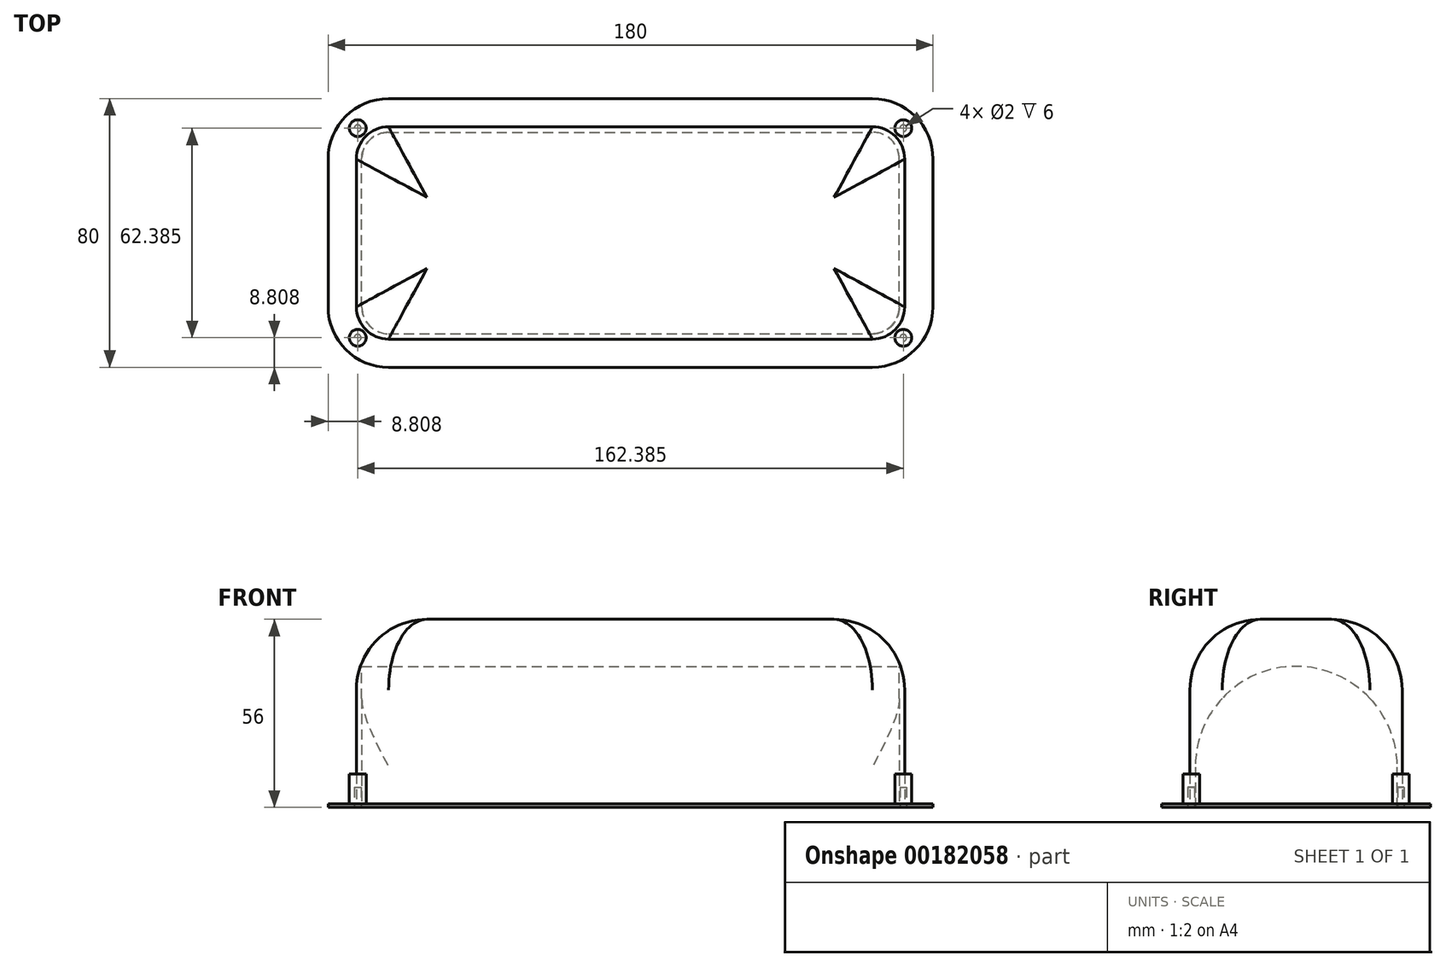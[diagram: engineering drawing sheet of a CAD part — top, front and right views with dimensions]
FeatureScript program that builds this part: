
annotation { "Feature Type Name" : "Feature", "Feature Type Description" : "" }
export const myFeature = defineFeature(function(context is Context, id is Id, definition is map)
    precondition{}
    {
        {
            var Q0;
            Q0=qCreatedBy(makeId("Top.planeOp"),FACE);
            var sketch = newSketch(context, id + "F0", { "sketchPlane" : qUnion([Q0])});
            skLineSegment(sketch, "E0.bottom", {"start": v(72, -40) * mm, "end": v(-72, -40) * mm});
            skLineSegment(sketch, "E0.top", {"start": v(72, 40) * mm, "end": v(-72, 40) * mm});
            skLineSegment(sketch, "E0.left", {"start": v(90, -22) * mm, "end": v(90, 22) * mm});
            skLineSegment(sketch, "E0.right", {"start": v(-90, -22) * mm, "end": v(-90, 22) * mm});
            skPoint(sketch, "E0.middle", {"position": v(0, 0) * mm});
            skPoint(sketch, "E1.visualSharp", {"position": v(-90, 40) * mm});
            skArc(sketch, "E1.filletArc", {"start": v(-72, 40) * mm, "mid": v(-84.73, 34.73) * mm, "end": v(-90, 22) * mm});
            skPoint(sketch, "E2.visualSharp", {"position": v(-90, -40) * mm});
            skArc(sketch, "E2.filletArc", {"start": v(-90, -22) * mm, "mid": v(-84.73, -34.73) * mm, "end": v(-72, -40) * mm});
            skPoint(sketch, "E3.visualSharp", {"position": v(90, -40) * mm});
            skArc(sketch, "E3.filletArc", {"start": v(72, -40) * mm, "mid": v(84.73, -34.73) * mm, "end": v(90, -22) * mm});
            skPoint(sketch, "E4.visualSharp", {"position": v(90, 40) * mm});
            skArc(sketch, "E4.filletArc", {"start": v(90, 22) * mm, "mid": v(84.73, 34.73) * mm, "end": v(72, 40) * mm});
            skLineSegment(sketch, "E5.0", {"start": v(72, 30) * mm, "end": v(-72, 30) * mm});
            skArc(sketch, "E5.1", {"start": v(80, 22) * mm, "mid": v(77.66, 27.66) * mm, "end": v(72, 30) * mm});
            skArc(sketch, "E5.2", {"start": v(-72, 30) * mm, "mid": v(-77.66, 27.66) * mm, "end": v(-80, 22) * mm});
            skLineSegment(sketch, "E5.3", {"start": v(80, -22) * mm, "end": v(80, 22) * mm});
            skLineSegment(sketch, "E5.4", {"start": v(-80, -22) * mm, "end": v(-80, 22) * mm});
            skArc(sketch, "E5.5", {"start": v(-80, -22) * mm, "mid": v(-77.66, -27.66) * mm, "end": v(-72, -30) * mm});
            skLineSegment(sketch, "E5.6", {"start": v(72, -30) * mm, "end": v(-72, -30) * mm});
            skArc(sketch, "E5.7", {"start": v(72, -30) * mm, "mid": v(77.66, -27.66) * mm, "end": v(80, -22) * mm});
            skSolve(sketch);
        }
        {
            var Q0;
            Q0 = qSketchRegion(id + "F0", true);
            extrude(context, id + "F1", {"entities" : qUnion([Q0]), "depth" : 1 * mm});
        }
        {
            var Q0;
            Q0=makeQuery(id+"F1.opExtrude","CAP_FACE",FACE,{"disambiguationData":[OSD([sQuery(id+"F0.wireOp",EDGE,"E0.bottom"),sQuery(id+"F0.wireOp",EDGE,"E0.top"),sQuery(id+"F0.wireOp",EDGE,"E0.left"),sQuery(id+"F0.wireOp",EDGE,"E0.right"),sQuery(id+"F0.wireOp",EDGE,"E1.filletArc"),sQuery(id+"F0.wireOp",EDGE,"E2.filletArc"),sQuery(id+"F0.wireOp",EDGE,"E3.filletArc"),sQuery(id+"F0.wireOp",EDGE,"E4.filletArc"),sQuery(id+"F0.wireOp",EDGE,"E5.0"),sQuery(id+"F0.wireOp",EDGE,"E5.1"),sQuery(id+"F0.wireOp",EDGE,"E5.2"),sQuery(id+"F0.wireOp",EDGE,"E5.3"),sQuery(id+"F0.wireOp",EDGE,"E5.4"),sQuery(id+"F0.wireOp",EDGE,"E5.5"),sQuery(id+"F0.wireOp",EDGE,"E5.6"),sQuery(id+"F0.wireOp",EDGE,"E5.7")])],"isStart":false});
            var sketch = newSketch(context, id + "F2", { "sketchPlane" : qUnion([Q0])});
            skLineSegment(sketch, "E6.0", {"start": v(72, 30) * mm, "end": v(-72, 30) * mm});
            skArc(sketch, "E7.0", {"start": v(-72, 30) * mm, "mid": v(-77.66, 27.66) * mm, "end": v(-80, 22) * mm});
            skLineSegment(sketch, "E8.0", {"start": v(-80, -22) * mm, "end": v(-80, 22) * mm});
            skArc(sketch, "E9.0", {"start": v(-80, -22) * mm, "mid": v(-77.66, -27.66) * mm, "end": v(-72, -30) * mm});
            skLineSegment(sketch, "E10.0", {"start": v(72, -30) * mm, "end": v(-72, -30) * mm});
            skArc(sketch, "E11.0", {"start": v(72, -30) * mm, "mid": v(77.66, -27.66) * mm, "end": v(80, -22) * mm});
            skLineSegment(sketch, "E12.0", {"start": v(80, -22) * mm, "end": v(80, 22) * mm});
            skArc(sketch, "E13.0", {"start": v(80, 22) * mm, "mid": v(77.66, 27.66) * mm, "end": v(72, 30) * mm});
            skArc(sketch, "E14.0", {"start": v(81.6, 22) * mm, "mid": v(78.79, 28.79) * mm, "end": v(72, 31.6) * mm});
            skLineSegment(sketch, "E14.1", {"start": v(81.6, -22) * mm, "end": v(81.6, 22) * mm});
            skLineSegment(sketch, "E14.2", {"start": v(72, 31.6) * mm, "end": v(-72, 31.6) * mm});
            skArc(sketch, "E14.3", {"start": v(72, -31.6) * mm, "mid": v(78.79, -28.79) * mm, "end": v(81.6, -22) * mm});
            skArc(sketch, "E14.4", {"start": v(-72, 31.6) * mm, "mid": v(-78.79, 28.79) * mm, "end": v(-81.6, 22) * mm});
            skLineSegment(sketch, "E14.5", {"start": v(-81.6, -22) * mm, "end": v(-81.6, 22) * mm});
            skArc(sketch, "E14.6", {"start": v(-81.6, -22) * mm, "mid": v(-78.79, -28.79) * mm, "end": v(-72, -31.6) * mm});
            skLineSegment(sketch, "E14.7", {"start": v(72, -31.6) * mm, "end": v(-72, -31.6) * mm});
            skArc(sketch, "E15.0", {"start": v(-85, -22) * mm, "mid": v(-81.2, -31.2) * mm, "end": v(-72, -35) * mm});
            skLineSegment(sketch, "E15.1", {"start": v(-85, 22) * mm, "end": v(-85, -22) * mm});
            skLineSegment(sketch, "E15.2", {"start": v(-72, -35) * mm, "end": v(72, -35) * mm});
            skArc(sketch, "E15.3", {"start": v(-72, 35) * mm, "mid": v(-81.2, 31.2) * mm, "end": v(-85, 22) * mm});
            skArc(sketch, "E15.4", {"start": v(72, -35) * mm, "mid": v(81.2, -31.2) * mm, "end": v(85, -22) * mm});
            skLineSegment(sketch, "E15.5", {"start": v(85, -22) * mm, "end": v(85, 22) * mm});
            skArc(sketch, "E15.6", {"start": v(85, 22) * mm, "mid": v(81.2, 31.2) * mm, "end": v(72, 35) * mm});
            skLineSegment(sketch, "E15.7", {"start": v(72, 35) * mm, "end": v(-72, 35) * mm});
            skSolve(sketch);
        }
        {
            var Q0;
            Q0=makeQuery(id+"F2.imprint","IMPRINT",FACE,{"disambiguationData":[TD([[makeQuery(id+"F2.imprint","IMPRINT",EDGE,{"derivedFrom":sQuery(id+"F2.wireOp",EDGE,"E6.0")}),-1.0]])]});
            extrude(context, id + "F3", {"entities" : qUnion([Q0]), "operationType" : NewBodyOperationType.ADD, "depth" : 55 * mm});
        }
        {
            var Q0;
            Q0=makeQuery(id+"F1.opExtrude","CAP_FACE",FACE,{"disambiguationData":[OSD([sQuery(id+"F0.wireOp",EDGE,"E0.bottom"),sQuery(id+"F0.wireOp",EDGE,"E0.top"),sQuery(id+"F0.wireOp",EDGE,"E0.left"),sQuery(id+"F0.wireOp",EDGE,"E0.right"),sQuery(id+"F0.wireOp",EDGE,"E1.filletArc"),sQuery(id+"F0.wireOp",EDGE,"E2.filletArc"),sQuery(id+"F0.wireOp",EDGE,"E3.filletArc"),sQuery(id+"F0.wireOp",EDGE,"E4.filletArc"),sQuery(id+"F0.wireOp",EDGE,"E5.0"),sQuery(id+"F0.wireOp",EDGE,"E5.1"),sQuery(id+"F0.wireOp",EDGE,"E5.2"),sQuery(id+"F0.wireOp",EDGE,"E5.3"),sQuery(id+"F0.wireOp",EDGE,"E5.4"),sQuery(id+"F0.wireOp",EDGE,"E5.5"),sQuery(id+"F0.wireOp",EDGE,"E5.6"),sQuery(id+"F0.wireOp",EDGE,"E5.7")])],"isStart":true});
            var sketch = newSketch(context, id + "F4", { "sketchPlane" : qUnion([Q0])});
            skLineSegment(sketch, "E16", {"start": v(-77.66, -27.66) * mm, "end": v(-84.73, -34.73) * mm});
            skLineSegment(sketch, "E17", {"start": v(77.66, -27.66) * mm, "end": v(84.73, -34.73) * mm});
            skLineSegment(sketch, "E18", {"start": v(77.66, 27.66) * mm, "end": v(84.73, 34.73) * mm});
            skLineSegment(sketch, "E19", {"start": v(-77.66, 27.66) * mm, "end": v(-84.73, 34.73) * mm});
            skCircle(sketch, "E20", {"center": v(81.2, -31.2) * mm, "radius": 2.5 * mm});
            skCircle(sketch, "E21", {"center": v(-81.2, -31.2) * mm, "radius": 2.5 * mm});
            skCircle(sketch, "E22", {"center": v(81.2, 31.2) * mm, "radius": 2.5 * mm});
            skCircle(sketch, "E23", {"center": v(-81.2, 31.2) * mm, "radius": 2.5 * mm});
            skSolve(sketch);
        }
        {
            var Q0;
            Q0 = qSketchRegion(id + "F4", true);
            extrude(context, id + "F5", {"entities" : qUnion([Q0]), "operationType" : NewBodyOperationType.ADD, "oppositeDirection" : true, "depth" : 10 * mm});
        }
        {
            var Q0;
            Q0=qCreatedBy(makeId("Right.planeOp"),FACE);
            var sketch = newSketch(context, id + "F6", { "sketchPlane" : qUnion([Q0])});
            skLineSegment(sketch, "E24.0", {"start": v(-22, 0) * mm, "end": v(22, 0) * mm});
            skLineSegment(sketch, "E25.0", {"start": v(-30, 0) * mm, "end": v(-22, 0) * mm});
            skLineSegment(sketch, "E26.0", {"start": v(22, 0) * mm, "end": v(30, 0) * mm});
            skLineSegment(sketch, "E27", {"start": v(0, 0) * mm, "end": v(0, 42) * mm});
            skLineSegment(sketch, "E28", {"start": v(-30, 0) * mm, "end": v(-30, 2) * mm});
            skLineSegment(sketch, "E29", {"start": v(-30, 2) * mm, "end": v(-30, 12) * mm});
            skLineSegment(sketch, "E30", {"start": v(0, 42) * mm, "end": v(0, 42) * mm});
            skLineSegment(sketch, "E31", {"start": v(30, 12) * mm, "end": v(30, 2) * mm});
            skLineSegment(sketch, "E32", {"start": v(30, 2) * mm, "end": v(30, 0) * mm});
            skPoint(sketch, "E33.visualSharp", {"position": v(-30, 42) * mm});
            skArc(sketch, "E33.filletArc", {"start": v(0, 42) * mm, "mid": v(-21.21, 33.21) * mm, "end": v(-30, 12) * mm});
            skPoint(sketch, "E34.visualSharp", {"position": v(30, 42) * mm});
            skArc(sketch, "E34.filletArc", {"start": v(30, 12) * mm, "mid": v(21.21, 33.21) * mm, "end": v(0, 42) * mm});
            skLineSegment(sketch, "E35", {"start": v(-30, 12) * mm, "end": v(-30, 56) * mm});
            skLineSegment(sketch, "E36", {"start": v(-30, 56) * mm, "end": v(30, 56) * mm});
            skLineSegment(sketch, "E37", {"start": v(30, 56) * mm, "end": v(30, 12) * mm});
            skSolve(sketch);
        }
        {
            var Q0;
            Q0=makeQuery(id+"F6.imprint","IMPRINT",FACE,{"disambiguationData":[TD([[makeQuery(id+"F6.imprint","IMPRINT",EDGE,{"derivedFrom":sQuery(id+"F6.wireOp",EDGE,"E33.filletArc")}),-1.0]])]});
            extrude(context, id + "F7", {"entities" : qUnion([Q0]), "operationType" : NewBodyOperationType.ADD, "oppositeDirection" : true, "depth" : 3.2 * mm, "hasSecondDirection" : true, "secondDirectionOppositeDirection" : false, "secondDirectionDepth" : 3.2 * mm});
        }
        {
            var Q0;
            Q0=makeQuery(id+"F7.boolean.opBoolean","MERGE",FACE,{"derivedFrom":[makeQuery(id+"F3.opExtrude","CAP_FACE",FACE,{"disambiguationData":[OSD([sQuery(id+"F2.wireOp",EDGE,"E6.0"),sQuery(id+"F2.wireOp",EDGE,"E7.0"),sQuery(id+"F2.wireOp",EDGE,"E8.0"),sQuery(id+"F2.wireOp",EDGE,"E9.0"),sQuery(id+"F2.wireOp",EDGE,"E10.0"),sQuery(id+"F2.wireOp",EDGE,"E11.0"),sQuery(id+"F2.wireOp",EDGE,"E12.0"),sQuery(id+"F2.wireOp",EDGE,"E13.0"),sQuery(id+"F2.wireOp",EDGE,"E14.0"),sQuery(id+"F2.wireOp",EDGE,"E14.1"),sQuery(id+"F2.wireOp",EDGE,"E14.2"),sQuery(id+"F2.wireOp",EDGE,"E14.3"),sQuery(id+"F2.wireOp",EDGE,"E14.4"),sQuery(id+"F2.wireOp",EDGE,"E14.5"),sQuery(id+"F2.wireOp",EDGE,"E14.6"),sQuery(id+"F2.wireOp",EDGE,"E14.7")])],"isStart":false}),makeQuery(id+"F7.opExtrude","SWEPT_FACE",FACE,{"disambiguationData":[OSD([sQuery(id+"F6.wireOp",EDGE,"E36")])]})]});
            var sketch = newSketch(context, id + "F8", { "sketchPlane" : qUnion([Q0])});
            skArc(sketch, "E38.0", {"start": v(72, -31.6) * mm, "mid": v(78.79, -28.79) * mm, "end": v(81.6, -22) * mm});
            skLineSegment(sketch, "E39.0", {"start": v(72, -31.6) * mm, "end": v(-72, -31.6) * mm});
            skLineSegment(sketch, "E40.0", {"start": v(81.6, -22) * mm, "end": v(81.6, 22) * mm});
            skArc(sketch, "E41.0", {"start": v(81.6, 22) * mm, "mid": v(78.79, 28.79) * mm, "end": v(72, 31.6) * mm});
            skLineSegment(sketch, "E42.0", {"start": v(72, 31.6) * mm, "end": v(-72, 31.6) * mm});
            skArc(sketch, "E43.0", {"start": v(-72, 31.6) * mm, "mid": v(-78.79, 28.79) * mm, "end": v(-81.6, 22) * mm});
            skLineSegment(sketch, "E44.0", {"start": v(-81.6, -22) * mm, "end": v(-81.6, 22) * mm});
            skArc(sketch, "E45.0", {"start": v(-81.6, -22) * mm, "mid": v(-78.79, -28.79) * mm, "end": v(-72, -31.6) * mm});
            skSolve(sketch);
        }
        {
            var Q0;
            Q0=makeQuery(id+"F1.opExtrude","CAP_FACE",FACE,{"disambiguationData":[OSD([sQuery(id+"F0.wireOp",EDGE,"E0.bottom"),sQuery(id+"F0.wireOp",EDGE,"E0.top"),sQuery(id+"F0.wireOp",EDGE,"E0.left"),sQuery(id+"F0.wireOp",EDGE,"E0.right"),sQuery(id+"F0.wireOp",EDGE,"E1.filletArc"),sQuery(id+"F0.wireOp",EDGE,"E2.filletArc"),sQuery(id+"F0.wireOp",EDGE,"E3.filletArc"),sQuery(id+"F0.wireOp",EDGE,"E4.filletArc"),sQuery(id+"F0.wireOp",EDGE,"E5.0"),sQuery(id+"F0.wireOp",EDGE,"E5.1"),sQuery(id+"F0.wireOp",EDGE,"E5.2"),sQuery(id+"F0.wireOp",EDGE,"E5.3"),sQuery(id+"F0.wireOp",EDGE,"E5.4"),sQuery(id+"F0.wireOp",EDGE,"E5.5"),sQuery(id+"F0.wireOp",EDGE,"E5.6"),sQuery(id+"F0.wireOp",EDGE,"E5.7")])],"isStart":true});
            var sketch = newSketch(context, id + "F9", { "sketchPlane" : qUnion([Q0])});
            skLineSegment(sketch, "E46.0", {"start": v(72, 40) * mm, "end": v(-72, 40) * mm});
            skArc(sketch, "E47.0", {"start": v(-90, 22) * mm, "mid": v(-84.73, 34.73) * mm, "end": v(-72, 40) * mm});
            skLineSegment(sketch, "E48.0", {"start": v(-90, 22) * mm, "end": v(-90, -22) * mm});
            skArc(sketch, "E49.0", {"start": v(-72, -40) * mm, "mid": v(-84.73, -34.73) * mm, "end": v(-90, -22) * mm});
            skLineSegment(sketch, "E50.0", {"start": v(72, -40) * mm, "end": v(-72, -40) * mm});
            skArc(sketch, "E51.0", {"start": v(90, -22) * mm, "mid": v(84.73, -34.73) * mm, "end": v(72, -40) * mm});
            skLineSegment(sketch, "E52.0", {"start": v(90, 22) * mm, "end": v(90, -22) * mm});
            skArc(sketch, "E53.0", {"start": v(72, 40) * mm, "mid": v(84.73, 34.73) * mm, "end": v(90, 22) * mm});
            skArc(sketch, "E54.0", {"start": v(72, 40.8) * mm, "mid": v(85.3, 35.3) * mm, "end": v(90.8, 22) * mm});
            skLineSegment(sketch, "E54.1", {"start": v(90.8, 22) * mm, "end": v(90.8, -22) * mm});
            skLineSegment(sketch, "E54.2", {"start": v(72, 40.8) * mm, "end": v(-72, 40.8) * mm});
            skArc(sketch, "E54.3", {"start": v(90.8, -22) * mm, "mid": v(85.3, -35.3) * mm, "end": v(72, -40.8) * mm});
            skArc(sketch, "E54.4", {"start": v(-90.8, 22) * mm, "mid": v(-85.3, 35.3) * mm, "end": v(-72, 40.8) * mm});
            skLineSegment(sketch, "E54.5", {"start": v(-90.8, 22) * mm, "end": v(-90.8, -22) * mm});
            skArc(sketch, "E54.6", {"start": v(-72, -40.8) * mm, "mid": v(-85.3, -35.3) * mm, "end": v(-90.8, -22) * mm});
            skLineSegment(sketch, "E54.7", {"start": v(72, -40.8) * mm, "end": v(-72, -40.8) * mm});
            skSolve(sketch);
        }
        {
            var Q0;
            Q0=makeQuery(id+"FBeGWCSvGBcqAvT_1.boolean.opBoolean","MERGE",FACE,{"derivedFrom":[makeQuery(id+"F1.opExtrude","CAP_FACE",FACE,{"disambiguationData":[OSD([sQuery(id+"F0.wireOp",EDGE,"E0.bottom"),sQuery(id+"F0.wireOp",EDGE,"E0.top"),sQuery(id+"F0.wireOp",EDGE,"E0.left"),sQuery(id+"F0.wireOp",EDGE,"E0.right"),sQuery(id+"F0.wireOp",EDGE,"E1.filletArc"),sQuery(id+"F0.wireOp",EDGE,"E2.filletArc"),sQuery(id+"F0.wireOp",EDGE,"E3.filletArc"),sQuery(id+"F0.wireOp",EDGE,"E4.filletArc"),sQuery(id+"F0.wireOp",EDGE,"E5.0"),sQuery(id+"F0.wireOp",EDGE,"E5.1"),sQuery(id+"F0.wireOp",EDGE,"E5.2"),sQuery(id+"F0.wireOp",EDGE,"E5.3"),sQuery(id+"F0.wireOp",EDGE,"E5.4"),sQuery(id+"F0.wireOp",EDGE,"E5.5"),sQuery(id+"F0.wireOp",EDGE,"E5.6"),sQuery(id+"F0.wireOp",EDGE,"E5.7")])],"isStart":true}),makeQuery(id+"FBeGWCSvGBcqAvT_1.opExtrude","CAP_FACE",FACE,{"disambiguationData":[OSD([sQuery(id+"F9.wireOp",EDGE,"E46.0"),sQuery(id+"F9.wireOp",EDGE,"E47.0"),sQuery(id+"F9.wireOp",EDGE,"E48.0"),sQuery(id+"F9.wireOp",EDGE,"E49.0"),sQuery(id+"F9.wireOp",EDGE,"E50.0"),sQuery(id+"F9.wireOp",EDGE,"E51.0"),sQuery(id+"F9.wireOp",EDGE,"E52.0"),sQuery(id+"F9.wireOp",EDGE,"E53.0"),sQuery(id+"F9.wireOp",EDGE,"E54.0"),sQuery(id+"F9.wireOp",EDGE,"E54.1"),sQuery(id+"F9.wireOp",EDGE,"E54.2"),sQuery(id+"F9.wireOp",EDGE,"E54.3"),sQuery(id+"F9.wireOp",EDGE,"E54.4"),sQuery(id+"F9.wireOp",EDGE,"E54.5"),sQuery(id+"F9.wireOp",EDGE,"E54.6"),sQuery(id+"F9.wireOp",EDGE,"E54.7")])],"isStart":true})]});
            var sketch = newSketch(context, id + "F10", { "sketchPlane" : qUnion([Q0])});
            skCircle(sketch, "E55.0", {"center": v(-81.2, 31.2) * mm, "radius": 2.5 * mm});
            skCircle(sketch, "E56.0", {"center": v(-81.2, -31.2) * mm, "radius": 2.5 * mm});
            skCircle(sketch, "E57.0", {"center": v(81.2, 31.2) * mm, "radius": 2.5 * mm});
            skCircle(sketch, "E58.0", {"center": v(81.2, -31.2) * mm, "radius": 2.5 * mm});
            skCircle(sketch, "E59", {"center": v(81.2, 31.2) * mm, "radius": 1 * mm});
            skCircle(sketch, "E60", {"center": v(81.2, -31.2) * mm, "radius": 1 * mm});
            skCircle(sketch, "E61", {"center": v(-81.2, 31.2) * mm, "radius": 1 * mm});
            skCircle(sketch, "E62", {"center": v(-81.2, -31.2) * mm, "radius": 1 * mm});
            skSolve(sketch);
        }
        {
            var Q0;
            Q0=makeQuery(id+"F10.imprint","IMPRINT",FACE,{"disambiguationData":[TD([[makeQuery(id+"F10.imprint","IMPRINT",EDGE,{"derivedFrom":sQuery(id+"F10.wireOp",EDGE,"E61")}),1.0]])]});
            var Q1;
            Q1=makeQuery(id+"F10.imprint","IMPRINT",FACE,{"disambiguationData":[TD([[makeQuery(id+"F10.imprint","IMPRINT",EDGE,{"derivedFrom":sQuery(id+"F10.wireOp",EDGE,"E62")}),1.0]])]});
            var Q2;
            Q2=makeQuery(id+"F10.imprint","IMPRINT",FACE,{"disambiguationData":[TD([[makeQuery(id+"F10.imprint","IMPRINT",EDGE,{"derivedFrom":sQuery(id+"F10.wireOp",EDGE,"E60")}),1.0]])]});
            var Q3;
            Q3=makeQuery(id+"F10.imprint","IMPRINT",FACE,{"disambiguationData":[TD([[makeQuery(id+"F10.imprint","IMPRINT",EDGE,{"derivedFrom":sQuery(id+"F10.wireOp",EDGE,"E59")}),1.0]])]});
            extrude(context, id + "F11", {"entities" : qUnion([Q0, Q1, Q2, Q3]), "operationType" : NewBodyOperationType.REMOVE, "oppositeDirection" : true, "depth" : 6 * mm});
        }
        {
            var Q0;
            Q0=makeQuery(id+"F7.opExtrude","CAP_FACE",FACE,{"disambiguationData":[OSD([sQuery(id+"F6.wireOp",EDGE,"E33.filletArc"),sQuery(id+"F6.wireOp",EDGE,"E34.filletArc"),sQuery(id+"F6.wireOp",EDGE,"E35"),sQuery(id+"F6.wireOp",EDGE,"E36"),sQuery(id+"F6.wireOp",EDGE,"E37")])],"isStart":false});
            var sketch = newSketch(context, id + "F12", { "sketchPlane" : qUnion([Q0])});
            skArc(sketch, "E63.0.0", {"start": v(-30, 12) * mm, "mid": v(0, 42) * mm, "end": v(30, 12) * mm});
            skLineSegment(sketch, "E63.0.1", {"start": v(30, 12) * mm, "end": v(30, 56) * mm});
            skLineSegment(sketch, "E63.0.2", {"start": v(30, 56) * mm, "end": v(-30, 56) * mm});
            skLineSegment(sketch, "E63.0.3", {"start": v(-30, 56) * mm, "end": v(-30, 12) * mm});
            skSolve(sketch);
        }
        {
            var Q0;
            Q0 = qSketchRegion(id + "F12", true);
            var Q1;
            Q1=makeQuery(id+"F1.opExtrude","SWEPT_BODY",BODY,{"disambiguationData":[OSD([sQuery(id+"F0.wireOp",EDGE,"E0.bottom"),sQuery(id+"F0.wireOp",EDGE,"E0.top"),sQuery(id+"F0.wireOp",EDGE,"E0.left"),sQuery(id+"F0.wireOp",EDGE,"E0.right"),sQuery(id+"F0.wireOp",EDGE,"E1.filletArc"),sQuery(id+"F0.wireOp",EDGE,"E2.filletArc"),sQuery(id+"F0.wireOp",EDGE,"E3.filletArc"),sQuery(id+"F0.wireOp",EDGE,"E4.filletArc"),sQuery(id+"F0.wireOp",EDGE,"E5.0"),sQuery(id+"F0.wireOp",EDGE,"E5.1"),sQuery(id+"F0.wireOp",EDGE,"E5.2"),sQuery(id+"F0.wireOp",EDGE,"E5.3"),sQuery(id+"F0.wireOp",EDGE,"E5.4"),sQuery(id+"F0.wireOp",EDGE,"E5.5"),sQuery(id+"F0.wireOp",EDGE,"E5.6"),sQuery(id+"F0.wireOp",EDGE,"E5.7")])]});
            extrude(context, id + "F13", {"entities" : qUnion([Q0]), "operationType" : NewBodyOperationType.ADD, "endBound" : BoundingType.UP_TO_BODY, "endBoundEntityBody" : qUnion([Q1]), "depth" : 25 * mm});
        }
        {
            var Q0;
            Q0=makeQuery(id+"F7.opExtrude","CAP_FACE",FACE,{"disambiguationData":[OSD([sQuery(id+"F6.wireOp",EDGE,"E33.filletArc"),sQuery(id+"F6.wireOp",EDGE,"E34.filletArc"),sQuery(id+"F6.wireOp",EDGE,"E35"),sQuery(id+"F6.wireOp",EDGE,"E36"),sQuery(id+"F6.wireOp",EDGE,"E37")])],"isStart":true});
            var sketch = newSketch(context, id + "F14", { "sketchPlane" : qUnion([Q0])});
            skArc(sketch, "E64.0.0", {"start": v(-30, 12) * mm, "mid": v(0, 42) * mm, "end": v(30, 12) * mm});
            skLineSegment(sketch, "E64.0.1", {"start": v(30, 12) * mm, "end": v(30, 56) * mm});
            skLineSegment(sketch, "E64.0.2", {"start": v(30, 56) * mm, "end": v(-30, 56) * mm});
            skLineSegment(sketch, "E64.0.3", {"start": v(-30, 56) * mm, "end": v(-30, 12) * mm});
            skSolve(sketch);
        }
        {
            var Q0;
            Q0 = qSketchRegion(id + "F14", true);
            var Q1;
            Q1=makeQuery(id+"F1.opExtrude","SWEPT_BODY",BODY,{"disambiguationData":[OSD([sQuery(id+"F0.wireOp",EDGE,"E0.bottom"),sQuery(id+"F0.wireOp",EDGE,"E0.top"),sQuery(id+"F0.wireOp",EDGE,"E0.left"),sQuery(id+"F0.wireOp",EDGE,"E0.right"),sQuery(id+"F0.wireOp",EDGE,"E1.filletArc"),sQuery(id+"F0.wireOp",EDGE,"E2.filletArc"),sQuery(id+"F0.wireOp",EDGE,"E3.filletArc"),sQuery(id+"F0.wireOp",EDGE,"E4.filletArc"),sQuery(id+"F0.wireOp",EDGE,"E5.0"),sQuery(id+"F0.wireOp",EDGE,"E5.1"),sQuery(id+"F0.wireOp",EDGE,"E5.2"),sQuery(id+"F0.wireOp",EDGE,"E5.3"),sQuery(id+"F0.wireOp",EDGE,"E5.4"),sQuery(id+"F0.wireOp",EDGE,"E5.5"),sQuery(id+"F0.wireOp",EDGE,"E5.6"),sQuery(id+"F0.wireOp",EDGE,"E5.7")])]});
            extrude(context, id + "F15", {"entities" : qUnion([Q0]), "operationType" : NewBodyOperationType.ADD, "endBound" : BoundingType.UP_TO_BODY, "endBoundEntityBody" : qUnion([Q1]), "depth" : 25 * mm});
        }
        {
            var Q0;
            Q0=makeQuery(id+"F3.opExtrude","CAP_EDGE",EDGE,{"disambiguationData":[OSD([sQuery(id+"F2.wireOp",EDGE,"E14.2")])],"isStart":false});
            fillet(context, id + "F16", {"entities" : qUnion([Q0]), "radius" : 21 * mm, "tangentPropagation" : true, "allowEdgeOverflow" : false});
        }
    });
